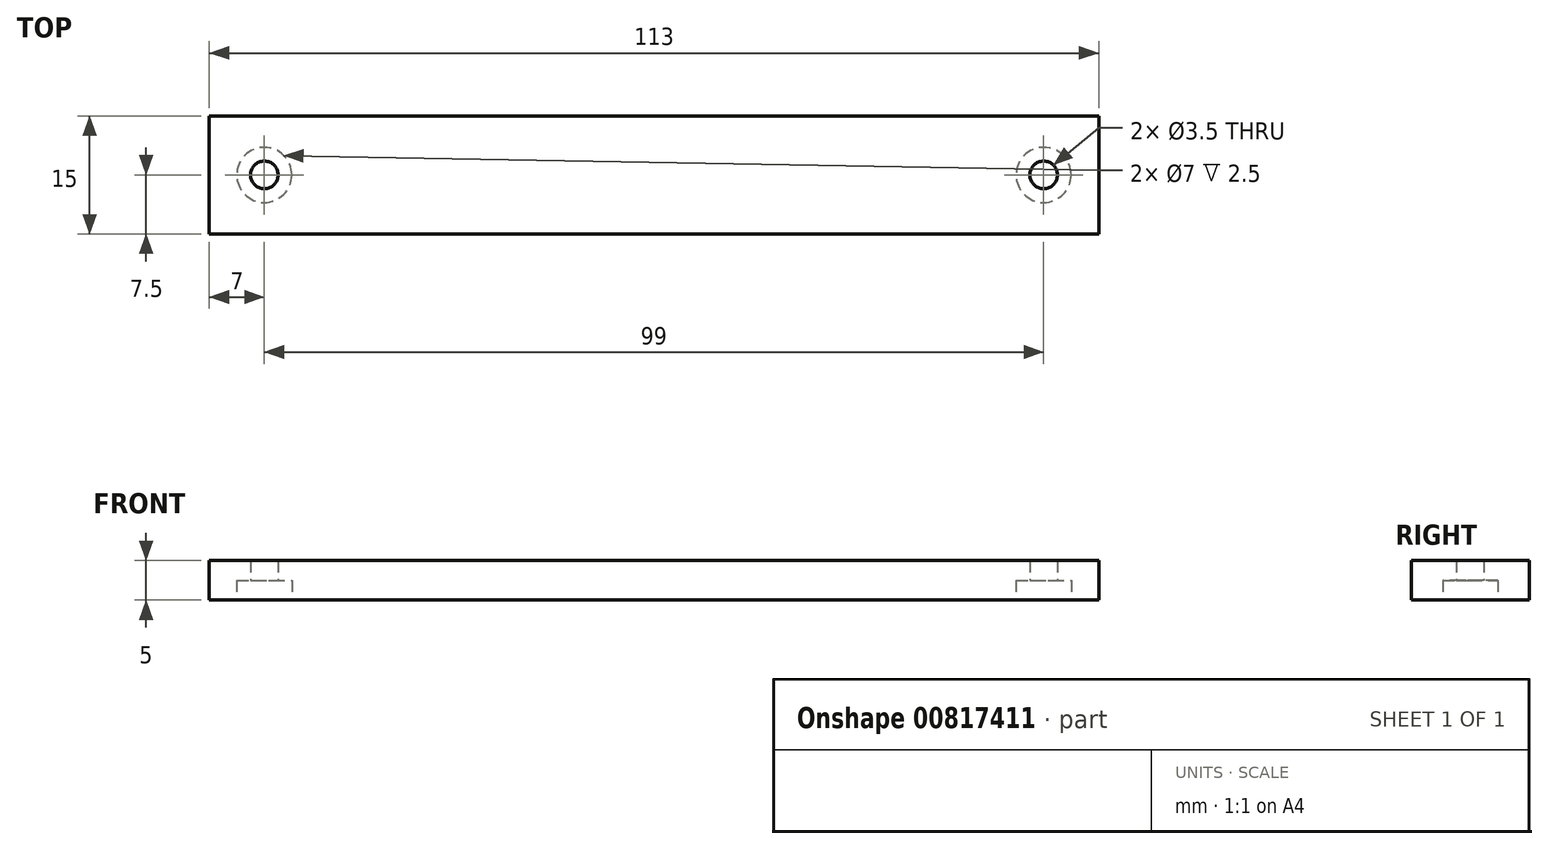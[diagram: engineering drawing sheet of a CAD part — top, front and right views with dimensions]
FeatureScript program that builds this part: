
annotation { "Feature Type Name" : "Feature", "Feature Type Description" : "" }
export const myFeature = defineFeature(function(context is Context, id is Id, definition is map)
    precondition{}
    {
        {
            var Q0;
            Q0=qCreatedBy(makeId("Top.planeOp"),FACE);
            var sketch = newSketch(context, id + "F0", { "sketchPlane" : qUnion([Q0])});
            skLineSegment(sketch, "E0.bottom", {"start": v(-56.5, -7.5) * mm, "end": v(56.5, -7.5) * mm});
            skLineSegment(sketch, "E0.top", {"start": v(-56.5, 7.5) * mm, "end": v(56.5, 7.5) * mm});
            skLineSegment(sketch, "E0.left", {"start": v(-56.5, -7.5) * mm, "end": v(-56.5, 7.5) * mm});
            skLineSegment(sketch, "E0.right", {"start": v(56.5, -7.5) * mm, "end": v(56.5, 7.5) * mm});
            skPoint(sketch, "E0.middle", {"position": v(0, 0) * mm});
            skLineSegment(sketch, "E1", {"start": v(-56.5, 0) * mm, "end": v(-49.5, 0) * mm});
            skCircle(sketch, "E2", {"center": v(-49.5, 0) * mm, "radius": 1.75 * mm});
            skCircle(sketch, "E3.MirrorC", {"center": v(49.5, 0) * mm, "radius": 1.75 * mm});
            skSolve(sketch);
        }
        {
            var Q0;
            Q0 = qSketchRegion(id + "F0", true);
            extrude(context, id + "F1", {"entities" : qUnion([Q0]), "depth" : 5 * mm, "offsetDistance" : 25 * mm});
        }
        {
            var Q0;
            Q0=makeQuery(id+"F1.opExtrude","CAP_FACE",FACE,{"disambiguationData":[OSD([sQuery(id+"F0.wireOp",EDGE,"E0.bottom"),sQuery(id+"F0.wireOp",EDGE,"E0.top"),sQuery(id+"F0.wireOp",EDGE,"E0.left"),sQuery(id+"F0.wireOp",EDGE,"E0.right"),sQuery(id+"F0.wireOp",EDGE,"E2"),sQuery(id+"F0.wireOp",EDGE,"E3.MirrorC")])],"isStart":true});
            var sketch = newSketch(context, id + "F2", { "sketchPlane" : qUnion([Q0])});
            skCircle(sketch, "E4", {"center": v(-49.5, 0) * mm, "radius": 3.5 * mm});
            skCircle(sketch, "E5.MirrorC", {"center": v(49.5, 0) * mm, "radius": 3.5 * mm});
            skSolve(sketch);
        }
        {
            var Q0;
            Q0 = qSketchRegion(id + "F2", true);
            extrude(context, id + "F3", {"entities" : qUnion([Q0]), "operationType" : NewBodyOperationType.REMOVE, "oppositeDirection" : true, "depth" : 2.5 * mm, "offsetDistance" : 25 * mm});
        }
    });
